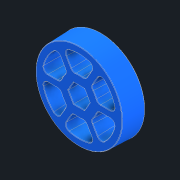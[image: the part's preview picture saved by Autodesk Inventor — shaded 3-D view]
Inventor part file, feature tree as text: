
AUTODESK INVENTOR PART (.ipt)
format: ipt  version: 2021 (Build 250183000, 183)  size: 787,968 bytes
history: native  units: in
note: dims shown in document units (in); Inventor stores cm internally (conversion verified against a paired STEP export)
features: fillet x1
ambient origin geometry x8: Origin, YZ Plane, XZ Plane, XY Plane, X Axis, Y Axis, Z Axis, Center Point
bodies: Solid1 (feature_tree)
feature tree (1):
  fillet  "Fillet3"  [1 undecoded]
note: 1 required parameter value undecoded (feature->parameter linkage not recoverable at this tier; creation-order binding heuristic only, values carry confidence <= 0.55)
